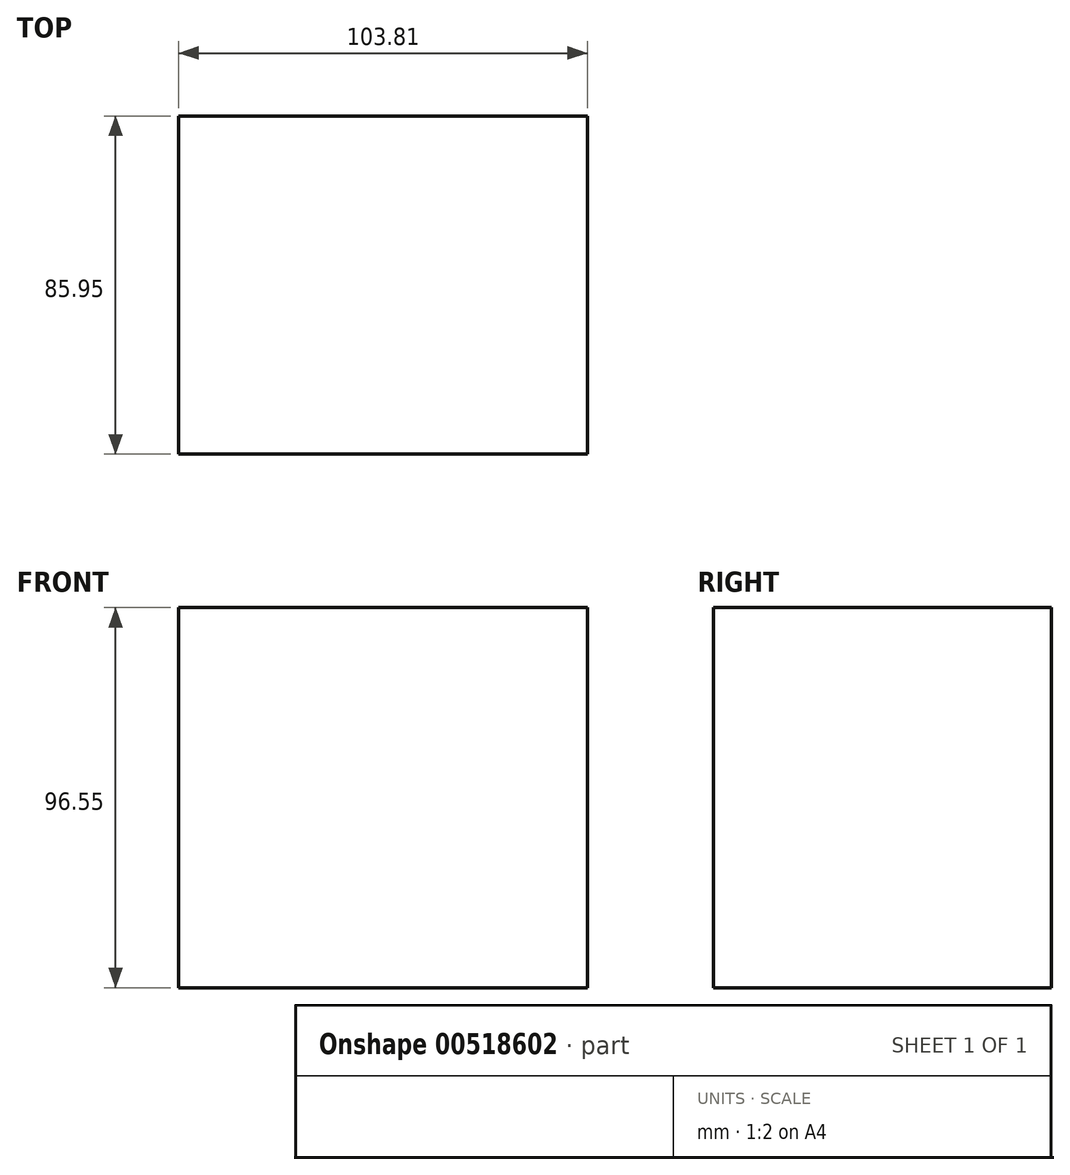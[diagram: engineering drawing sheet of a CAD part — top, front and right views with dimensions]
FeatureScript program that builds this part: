
annotation { "Feature Type Name" : "Feature", "Feature Type Description" : "" }
export const myFeature = defineFeature(function(context is Context, id is Id, definition is map)
    precondition{}
    {
        {
            var Q0;
            Q0=qCreatedBy(makeId("Front.planeOp"),FACE);
            var sketch = newSketch(context, id + "F0", { "sketchPlane" : qUnion([Q0])});
            skLineSegment(sketch, "E0.bottom", {"start": v(-51.43, 45.43) * mm, "end": v(52.38, 45.43) * mm});
            skLineSegment(sketch, "E0.top", {"start": v(-51.43, -51.12) * mm, "end": v(52.38, -51.12) * mm});
            skLineSegment(sketch, "E0.left", {"start": v(-51.43, 45.43) * mm, "end": v(-51.43, -51.12) * mm});
            skLineSegment(sketch, "E0.right", {"start": v(52.38, 45.43) * mm, "end": v(52.38, -51.12) * mm});
            skSolve(sketch);
        }
        {
            var Q0;
            Q0=makeQuery(id+"F0.imprint","IMPRINT",FACE,{"disambiguationData":[TD([[makeQuery(id+"F0.imprint","IMPRINT",EDGE,{"derivedFrom":sQuery(id+"F0.wireOp",EDGE,"E0.bottom")}),-1.0]])]});
            var Q1;
            Q1=sQuery(id+"F0.wireOp",EDGE,"E0.top");
            var Q2;
            Q2=sQuery(id+"F0.wireOp",EDGE,"E0.left");
            var Q3;
            Q3=sQuery(id+"F0.wireOp",EDGE,"E0.bottom");
            var Q4;
            Q4=sQuery(id+"F0.wireOp",EDGE,"E0.right");
            extrude(context, id + "F1", {"entities" : qUnion([Q0]), "bodyType" : ToolBodyType.SURFACE, "surfaceEntities" : qUnion([Q1, Q2, Q3, Q4]), "depth" : 85.95 * mm, "offsetDistance" : 25.4 * mm});
        }
        {
            var Q0;
            Q0=makeQuery(id+"F1.opExtrude","CAP_VERTEX",VERTEX,{"disambiguationData":[OSD([sQuery(id+"F0.wireOp",VERTEX,"E0.bottom.start")])],"isStart":false});
            var Q1;
            Q1=makeQuery(id+"F1.opExtrude","CAP_VERTEX",VERTEX,{"disambiguationData":[OSD([sQuery(id+"F0.wireOp",VERTEX,"E0.right.start")])],"isStart":true});
            var Q2;
            Q2=makeQuery(id+"F1.opExtrude","CAP_VERTEX",VERTEX,{"disambiguationData":[OSD([sQuery(id+"F0.wireOp",VERTEX,"E0.right.end")])],"isStart":false});
            cPlane(context, id + "F2", {"entities" : qUnion([Q0, Q1, Q2]), "cplaneType" : CPlaneType.THREE_POINT, "offset" : 254 * mm, "width" : 152.4 * mm, "height" : 152.4 * mm});
        }
    });
